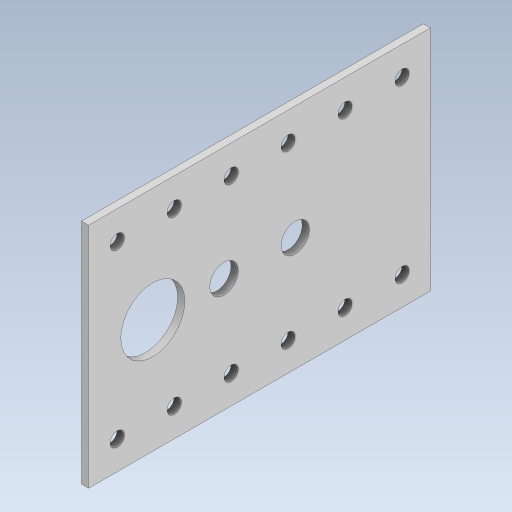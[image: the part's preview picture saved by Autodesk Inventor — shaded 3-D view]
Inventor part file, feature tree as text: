
AUTODESK INVENTOR PART (.ipt)
format: ipt  version: 2023 (Build 270158000, 158)  size: 141,312 bytes
history: native  units: in
note: dims shown in document units (in); Inventor stores cm internally (conversion verified against a paired STEP export)
features: extrude x1, sketch x1
ambient origin geometry x8: Origin, YZ Plane, XZ Plane, XY Plane, X Axis, Y Axis, Z Axis, Center Point
bodies: Solid1 (feature_tree)
feature tree (2):
  extrude  "Extrusion1"  Depth=6.0in
  sketch  "Sketch1"  dims[d0=4.0in d1=6.0in d2=1.125in d3=0.5in d4=0.5in d5=1.125in d6=1.25in d7=1.25in d8=1.25in d9=0.25in d10=0.5in d11=0.5in d12=2.3622in d14=1.0in d15=0.7874in d17=3.0in d20=0.125in d21=0.0in d22=0.5in d23=0.0344in d24=0.5in d25=0.0344in]
